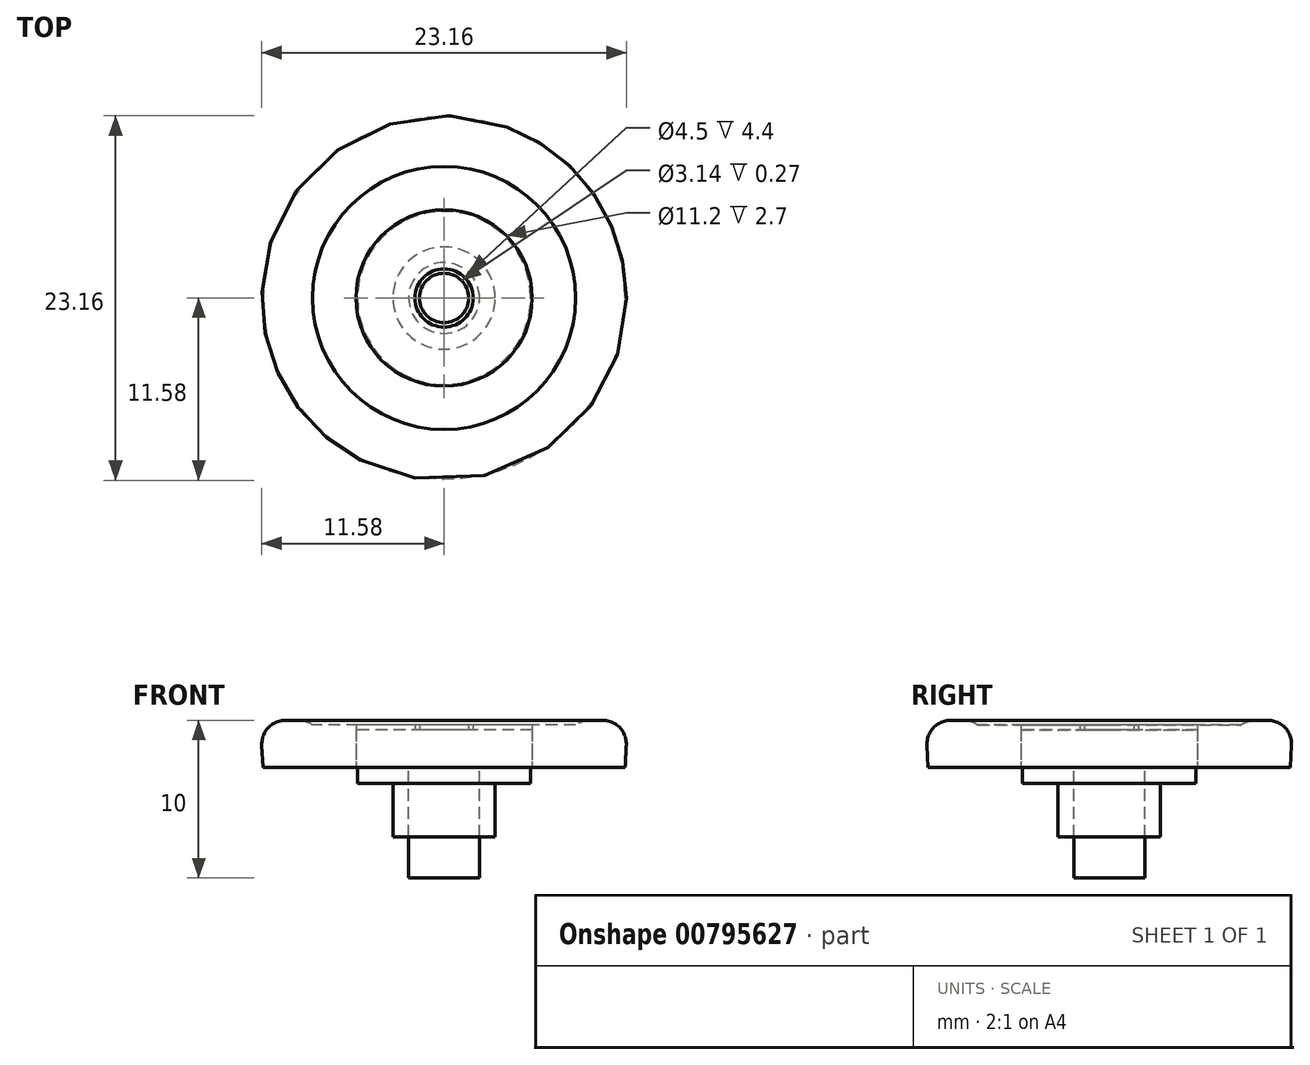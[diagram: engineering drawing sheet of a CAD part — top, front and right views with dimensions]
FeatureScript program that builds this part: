
annotation { "Feature Type Name" : "Feature", "Feature Type Description" : "" }
export const myFeature = defineFeature(function(context is Context, id is Id, definition is map)
    precondition{}
    {
        {
            var Q0;
            Q0=qCreatedBy(makeId("Top.planeOp"),FACE);
            var sketch = newSketch(context, id + "F0", { "sketchPlane" : qUnion([Q0])});
            skCircle(sketch, "E0", {"center": v(0, 0) * mm, "radius": 11.5 * mm});
            skCircle(sketch, "E1", {"center": v(0, 0) * mm, "radius": 8.5 * mm});
            skCircle(sketch, "E2", {"center": v(0, 0) * mm, "radius": 5.6 * mm});
            skSolve(sketch);
        }
        {
            var Q0;
            Q0=qSketchRegion(id+"F0",true);
            extrude(context, id + "F1", {"entities" : qUnion([Q0]), "depth" : 3 * mm, "offsetDistance" : 25 * mm, "hasDraft" : true, "draftAngle" : 3 * degree});
        }
        {
            var Q0;
            Q0=makeQuery(id+"F0.imprint","IMPRINT",FACE,{"disambiguationData":[TD([[makeQuery(id+"F0.imprint","IMPRINT",EDGE,{"derivedFrom":sQuery(id+"F0.wireOp",EDGE,"E1")}),1.0]])]});
            extrude(context, id + "F2", {"entities" : qUnion([Q0]), "operationType" : NewBodyOperationType.ADD, "depth" : 2.7 * mm, "offsetDistance" : 25 * mm});
        }
        {
            var Q0;
            Q0=makeQuery(id+"F0.imprint","IMPRINT",FACE,{"disambiguationData":[TD([[makeQuery(id+"F0.imprint","IMPRINT",EDGE,{"derivedFrom":sQuery(id+"F0.wireOp",EDGE,"sJWBEL4Q-zqKP-wKAH-Xvia-YZl9IQGTlxIB")}),1.0]])]});
            var Q1;
            Q1=makeQuery(id+"F0.imprint","IMPRINT",FACE,{"disambiguationData":[TD([[makeQuery(id+"F0.imprint","IMPRINT",EDGE,{"derivedFrom":sQuery(id+"F0.wireOp",EDGE,"W3Ua214L-QGfU-jLto-IY45-T6SqmYm5Pf0N")}),1.0]])]});
            var Q2;
            Q2=makeQuery(id+"F0.imprint","IMPRINT",FACE,{"disambiguationData":[TD([[makeQuery(id+"F0.imprint","IMPRINT",EDGE,{"derivedFrom":sQuery(id+"F0.wireOp",EDGE,"KE1PqsyT-DHGX-8diU-NURI-yFHnlOPL5x9j")}),1.0]])]});
            var Q3;
            Q3=makeQuery(id+"F0.imprint","IMPRINT",FACE,{"disambiguationData":[TD([[makeQuery(id+"F0.imprint","IMPRINT",EDGE,{"derivedFrom":sQuery(id+"F0.wireOp",EDGE,"93cc1e78-3582-4651-860f-33596dd8aeea")}),1.0]])]});
            var Q4;
            Q4=makeQuery(id+"F0.imprint","IMPRINT",FACE,{"disambiguationData":[TD([[makeQuery(id+"F0.imprint","IMPRINT",EDGE,{"derivedFrom":sQuery(id+"F0.wireOp",EDGE,"580936a7-a73b-495c-908d-01e9c6adc14b")}),1.0]])]});
            var Q5;
            Q5=makeQuery(id+"F0.imprint","IMPRINT",FACE,{"disambiguationData":[TD([[makeQuery(id+"F0.imprint","IMPRINT",EDGE,{"derivedFrom":sQuery(id+"F0.wireOp",EDGE,"914aee80-40cc-4c9e-a0ba-7517bd072fba")}),1.0]])]});
            var Q6;
            Q6=makeQuery(id+"F0.imprint","IMPRINT",FACE,{"disambiguationData":[TD([[makeQuery(id+"F0.imprint","IMPRINT",EDGE,{"derivedFrom":sQuery(id+"F0.wireOp",EDGE,"tJGHLqfq-XDhS-PHHt-wrfx-KiIFVS5NVcas")}),1.0]])]});
            var Q7;
            Q7=makeQuery(id+"F0.imprint","IMPRINT",FACE,{"disambiguationData":[TD([[makeQuery(id+"F0.imprint","IMPRINT",EDGE,{"derivedFrom":sQuery(id+"F0.wireOp",EDGE,"QfYnkFk0-Tl5y-BypX-IXop-PRvAgd9sKDpf")}),1.0]])]});
            var Q8;
            Q8=makeQuery(id+"F0.imprint","IMPRINT",FACE,{"disambiguationData":[TD([[makeQuery(id+"F0.imprint","IMPRINT",EDGE,{"derivedFrom":sQuery(id+"F0.wireOp",EDGE,"Y070iHcx-JKvN-373v-bcgJ-Ptq9Z7jqXRuu")}),1.0]])]});
            var Q9;
            {var subQ0=sQuery(id+"F0.wireOp",EDGE,"364aceb5-e4ae-42a2-838b-8d2f1a538a20");var subQ5=sQuery(id+"F0.wireOp",EDGE,"E2");var subQ8=makeQuery(id+"F0.imprint","INTERSECT",VERTEX,{"disambiguationData":[OD(0.0)],"derivedFrom":[subQ5,subQ0]});Q9=makeQuery(id+"F0.imprint","IMPRINT",FACE,{"disambiguationData":[TD([[makeQuery(id+"F0.imprint","IMPRINT",EDGE,{"disambiguationData":[TD([[subQ8,1.0]])],"derivedFrom":subQ5}),1.0]])]});}
            var Q10;
            {var subQ1=sQuery(id+"F0.wireOp",EDGE,"E2");var subQ3=sQuery(id+"F0.wireOp",EDGE,"240fa6d0-75f4-4649-a5dc-fb8ea6b493ce");var subQ4=makeQuery(id+"F0.imprint","INTERSECT",VERTEX,{"disambiguationData":[OD(0.0)],"derivedFrom":[subQ1,subQ3]});Q10=makeQuery(id+"F0.imprint","IMPRINT",FACE,{"disambiguationData":[TD([[makeQuery(id+"F0.imprint","IMPRINT",EDGE,{"disambiguationData":[TD([[subQ4,-1.0]])],"derivedFrom":subQ1}),1.0]])]});}
            var Q11;
            {var subQ0=sQuery(id+"F0.wireOp",EDGE,"a4363b79-0781-4621-b503-21fbbac03dd4");Q11=makeQuery(id+"F0.imprint","IMPRINT",FACE,{"disambiguationData":[TD([[makeQuery(id+"F0.imprint","IMPRINT",EDGE,{"derivedFrom":subQ0}),1.0]])]});}
            var Q12;
            Q12=makeQuery(id+"F0.imprint","IMPRINT",FACE,{"disambiguationData":[TD([[makeQuery(id+"F0.imprint","IMPRINT",EDGE,{"derivedFrom":sQuery(id+"F0.wireOp",EDGE,"dakPGjOR-qgw5-qXTv-UFbR-eR2Q9f3JjfMY")}),1.0]])]});
            var Q13;
            Q13=makeQuery(id+"F0.imprint","IMPRINT",FACE,{"disambiguationData":[TD([[makeQuery(id+"F0.imprint","IMPRINT",EDGE,{"derivedFrom":sQuery(id+"F0.wireOp",EDGE,"c86a8116-1d08-438b-9353-779b471d0a26")}),-1.0]])]});
            var Q14;
            {var subQ5=sQuery(id+"F0.wireOp",EDGE,"240fa6d0-75f4-4649-a5dc-fb8ea6b493ce");Q14=makeQuery(id+"F0.imprint","IMPRINT",FACE,{"disambiguationData":[TD([[makeQuery(id+"F0.imprint","IMPRINT",EDGE,{"derivedFrom":subQ5}),-1.0]])]});}
            var Q15;
            {var subQ0=sQuery(id+"F0.wireOp",EDGE,"cf34df1f-d6ec-4883-8101-f005d7a4a38d");Q15=makeQuery(id+"F0.imprint","IMPRINT",FACE,{"disambiguationData":[TD([[makeQuery(id+"F0.imprint","IMPRINT",EDGE,{"derivedFrom":subQ0}),-1.0]])]});}
            extrude(context, id + "F3", {"entities" : qUnion([Q0, Q1, Q2, Q3, Q4, Q5, Q6, Q7, Q8, Q9, Q10, Q11, Q12, Q13, Q14, Q15]), "depth" : 2.4 * mm, "offsetDistance" : 25 * mm});
        }
        {
            var Q0;
            Q0=makeQuery(id+"F1.opExtrude","CAP_EDGE",EDGE,{"disambiguationData":[OSD([sQuery(id+"F0.wireOp",EDGE,"E1")])],"isStart":false});
            var Q1;
            Q1=makeQuery(id+"F1.opExtrude","CAP_EDGE",EDGE,{"disambiguationData":[OSD([sQuery(id+"F0.wireOp",EDGE,"E0")])],"isStart":false});
            fillet(context, id + "F4", {"entities" : qUnion([Q0, Q1]), "radius" : 1.5 * mm, "tangentPropagation" : true, "allowEdgeOverflow" : false});
        }
        {
            var Q0;
            Q0=qCreatedBy(makeId("Top.planeOp"),FACE);
            var sketch = newSketch(context, id + "F5", { "sketchPlane" : qUnion([Q0])});
            skCircle(sketch, "E3", {"center": v(0, 0) * mm, "radius": 5.5 * mm});
            skCircle(sketch, "E4", {"center": v(0, 0) * mm, "radius": 3.25 * mm});
            skCircle(sketch, "E5", {"center": v(0, 0) * mm, "radius": 2.25 * mm});
            skSolve(sketch);
        }
        {
            var Q0;
            Q0=qSketchRegion(id+"F5",true);
            extrude(context, id + "F6", {"entities" : qUnion([Q0]), "operationType" : NewBodyOperationType.ADD, "oppositeDirection" : true, "depth" : 1 * mm, "offsetDistance" : 25 * mm});
        }
        {
            var Q0;
            Q0=makeQuery(id+"F5.imprint","IMPRINT",FACE,{"disambiguationData":[TD([[makeQuery(id+"F5.imprint","IMPRINT",EDGE,{"derivedFrom":sQuery(id+"F5.wireOp",EDGE,"E4")}),1.0]])]});
            extrude(context, id + "F7", {"entities" : qUnion([Q0]), "operationType" : NewBodyOperationType.ADD, "oppositeDirection" : true, "depth" : 4.4 * mm, "offsetDistance" : 25 * mm});
        }
        {
            var Q0;
            Q0=makeQuery(id+"F5.imprint","IMPRINT",FACE,{"disambiguationData":[TD([[makeQuery(id+"F5.imprint","IMPRINT",EDGE,{"derivedFrom":sQuery(id+"F5.wireOp",EDGE,"E5")}),1.0]])]});
            extrude(context, id + "F8", {"entities" : qUnion([Q0]), "oppositeDirection" : true, "depth" : 7 * mm, "offsetDistance" : 25 * mm});
        }
        {
            var Q0;
            Q0=qCreatedBy(makeId("Top.planeOp"),FACE);
            cPlane(context, id + "F9", {"entities" : qUnion([Q0]), "cplaneType" : CPlaneType.OFFSET, "offset" : 2.4 * mm, "width" : 150 * mm, "height" : 150 * mm});
        }
        {
            var Q0;
            Q0=qCreatedBy(id+"F9.planeOp",FACE);
            var sketch = newSketch(context, id + "F10", { "sketchPlane" : qUnion([Q0])});
            skCircle(sketch, "E6", {"center": v(0, 0) * mm, "radius": 1.85 * mm});
            skCircle(sketch, "E7", {"center": v(0, 0) * mm, "radius": 1.57 * mm});
            skCircle(sketch, "E8", {"center": v(0, 0) * mm, "radius": 5.6 * mm});
            skFitSpline(sketch, "E9", {"points": [v(1.78, -0.5) * mm, v(1.79, -0.56) * mm, v(1.81, -0.61) * mm, v(1.9, -0.7) * mm, v(2.12, -0.88) * mm, v(2.47, -1.1) * mm, v(2.86, -1.37) * mm, v(3.48, -1.75) * mm, v(4.06, -2.14) * mm, v(4.51, -2.4) * mm, v(4.63, -2.44) * mm, v(4.76, -2.46) * mm, v(4.87, -2.44) * mm, v(4.98, -2.4) * mm, v(5.1, -2.3) * mm], "startDerivative": vector(-0.8, -2.81) * mm, "endDerivative": vector(1.02, 2.24) * mm});
            skFitSpline(sketch, "E10", {"points": [v(-1.07, -1.51) * mm, v(-1.2, -1.46) * mm, v(-1.28, -1.46) * mm, v(-1.4, -1.48) * mm, v(-1.66, -1.6) * mm, v(-2.02, -1.8) * mm, v(-2.43, -2.03) * mm, v(-3.06, -2.4) * mm, v(-3.68, -2.73) * mm, v(-4.11, -3) * mm, v(-4.22, -3.08) * mm, v(-4.3, -3.18) * mm, v(-4.36, -3.3) * mm, v(-4.37, -3.42) * mm, v(-4.3, -3.58) * mm], "startDerivative": vector(-2.5, 1.82) * mm, "endDerivative": vector(2.87, -3.5) * mm});
            skFitSpline(sketch, "E11", {"points": [v(0.97, -1.57) * mm, v(1.06, -1.54) * mm, v(1.16, -1.52) * mm, v(1.3, -1.5) * mm, v(1.46, -1.55) * mm, v(1.84, -1.76) * mm, v(2.37, -2.05) * mm, v(2.81, -2.3) * mm, v(3.45, -2.66) * mm, v(4, -2.98) * mm, v(4.14, -3.06) * mm, v(4.24, -3.15) * mm, v(4.3, -3.27) * mm, v(4.33, -3.38) * mm, v(4.31, -3.53) * mm, v(4.25, -3.64) * mm, v(4.25, -3.64) * mm], "startDerivative": vector(2.43, 1.54) * mm, "endDerivative": vector(0.65, 0.76) * mm});
            skCircle(sketch, "E12", {"center": v(2.1, -1.4) * mm, "radius": 0.22 * mm});
            skCircle(sketch, "E13", {"center": v(3.06, -1.98) * mm, "radius": 0.18 * mm});
            skCircle(sketch, "E14", {"center": v(3.83, -2.46) * mm, "radius": 0.14 * mm});
            skLineSegment(sketch, "E15", {"start": v(1.53, -1.04) * mm, "end": v(4.73, -3) * mm, "construction": true});
            skFitSpline(sketch, "E16", {"points": [v(-1.83, -0.27) * mm, v(-1.83, -0.48) * mm, v(-1.86, -0.55) * mm, v(-1.93, -0.65) * mm, v(-2.05, -0.77) * mm, v(-2.4, -1.03) * mm, v(-2.9, -1.37) * mm, v(-3.39, -1.67) * mm, v(-3.91, -2) * mm, v(-4.36, -2.26) * mm, v(-4.67, -2.42) * mm, v(-4.86, -2.46) * mm, v(-5, -2.43) * mm, v(-5.25, -1.96) * mm], "startDerivative": vector(1.36, -7.17) * mm, "endDerivative": vector(-3.92, 9.14) * mm});
            skCircle(sketch, "E17", {"center": v(-2.18, -1.4) * mm, "radius": 0.22 * mm});
            skCircle(sketch, "E18", {"center": v(-3.14, -1.99) * mm, "radius": 0.18 * mm});
            skCircle(sketch, "E19", {"center": v(-3.91, -2.46) * mm, "radius": 0.14 * mm});
            skLineSegment(sketch, "E20", {"start": v(-1.54, -1.02) * mm, "end": v(-4.76, -2.95) * mm, "construction": true});
            skFitSpline(sketch, "E21", {"points": [v(-0.72, 1.7) * mm, v(-0.59, 1.81) * mm, v(-0.52, 1.91) * mm, v(-0.47, 2.08) * mm, v(-0.46, 2.3) * mm, v(-0.45, 2.72) * mm, v(-0.44, 3.2) * mm, v(-0.44, 3.91) * mm, v(-0.42, 4.62) * mm, v(-0.44, 5.13) * mm, v(-0.47, 5.26) * mm, v(-0.51, 5.38) * mm, v(-0.59, 5.46) * mm, v(-0.7, 5.53) * mm, v(-0.82, 5.54) * mm], "startDerivative": vector(2.8, 0.8) * mm, "endDerivative": vector(-2.44, -0.32) * mm});
            skFitSpline(sketch, "E22", {"points": [v(0.74, 1.7) * mm, v(0.67, 1.75) * mm, v(0.6, 1.83) * mm, v(0.51, 1.94) * mm, v(0.47, 2.1) * mm, v(0.44, 2.53) * mm, v(0.43, 3.14) * mm, v(0.42, 3.65) * mm, v(0.4, 4.38) * mm, v(0.39, 5.1) * mm, v(0.4, 5.24) * mm, v(0.44, 5.37) * mm, v(0.5, 5.45) * mm, v(0.58, 5.5) * mm, v(0.67, 5.53) * mm, v(0.84, 5.54) * mm], "startDerivative": vector(-1.87, 1.36) * mm, "endDerivative": vector(4.35, -0.63) * mm});
            skCircle(sketch, "E23", {"center": v(0, 2.56) * mm, "radius": 0.22 * mm});
            skCircle(sketch, "E24", {"center": v(0, 3.73) * mm, "radius": 0.18 * mm});
            skCircle(sketch, "E25", {"center": v(0, 4.59) * mm, "radius": 0.14 * mm});
            skLineSegment(sketch, "E26", {"start": v(0, 1.85) * mm, "end": v(0, 5.6) * mm, "construction": true});
            skCircle(sketch, "E27", {"center": v(0, 0) * mm, "radius": 5.95 * mm});
            skFitSpline(sketch, "E28", {"points": [v(-1.05, -0.83) * mm, v(-1.13, -0.72) * mm, v(-1.22, -0.56) * mm, v(-1.28, -0.37) * mm, v(-1.3, -0.17) * mm, v(-1.32, 0.02) * mm, v(-1.3, 0.2) * mm, v(-1.22, 0.43) * mm, v(-1.13, 0.6) * mm, v(-1, 0.78) * mm, v(-0.85, 0.93) * mm, v(-0.72, 1.04) * mm, v(-0.56, 1.13) * mm, v(-0.45, 1.18) * mm, v(-0.45, 1.18) * mm], "startDerivative": vector(-1.28, 1.58) * mm, "endDerivative": vector(-0.6, -0.06) * mm});
            skFitSpline(sketch, "E29", {"points": [v(-0.64, 0.92) * mm, v(-0.75, 0.85) * mm, v(-0.84, 0.76) * mm, v(-0.93, 0.66) * mm, v(-1.01, 0.53) * mm, v(-1.08, 0.36) * mm, v(-1.1, 0.21) * mm, v(-1.12, 0.05) * mm, v(-1.12, -0.13) * mm], "startDerivative": vector(-1.01, -0.52) * mm, "endDerivative": vector(0, -1.33) * mm});
            skFitSpline(sketch, "E30", {"points": [v(-1.12, -0.13) * mm, v(-0.9, -0.13) * mm, v(-0.65, -0.13) * mm], "startDerivative": vector(0.46, 0) * mm, "endDerivative": vector(0.47, 0) * mm});
            skFitSpline(sketch, "E31", {"points": [v(-0.65, -0.13) * mm, v(-0.65, 0.18) * mm, v(-0.65, 0.52) * mm, v(-0.64, 0.92) * mm], "startDerivative": vector(0, 0.98) * mm, "endDerivative": vector(0.04, 1.13) * mm});
            skFitSpline(sketch, "E32", {"points": [v(-0.45, 1.18) * mm, v(-0.45, 0.64) * mm, v(-0.45, -0.19) * mm, v(-0.45, -0.76) * mm, v(-0.45, -1.2) * mm], "startDerivative": vector(0, -2.1) * mm, "endDerivative": vector(0, -2.03) * mm});
            skFitSpline(sketch, "E33", {"points": [v(-0.45, -1.2) * mm, v(-0.53, -1.16) * mm, v(-0.64, -1.11) * mm], "startDerivative": vector(-0.17, 0.1) * mm, "endDerivative": vector(-0.22, 0.1) * mm});
            skFitSpline(sketch, "E34", {"points": [v(-0.64, -1.11) * mm, v(-0.64, -0.76) * mm, v(-0.64, -0.5) * mm, v(-0.64, -0.29) * mm], "startDerivative": vector(0, 0.95) * mm, "endDerivative": vector(0, 0.7) * mm});
            skFitSpline(sketch, "E35", {"points": [v(-0.64, -0.29) * mm, v(-0.85, -0.29) * mm, v(-1.05, -0.29) * mm], "startDerivative": vector(-0.4, 0) * mm, "endDerivative": vector(-0.41, 0) * mm});
            skFitSpline(sketch, "E36", {"points": [v(-1.05, -0.29) * mm, v(-1.04, -0.4) * mm, v(-1.01, -0.5) * mm, v(-0.95, -0.6) * mm, v(-0.9, -0.68) * mm], "startDerivative": vector(0.02, -0.66) * mm, "endDerivative": vector(0.26, -0.3) * mm});
            skFitSpline(sketch, "E37", {"points": [v(-0.9, -0.68) * mm, v(-0.97, -0.75) * mm, v(-1.05, -0.83) * mm], "startDerivative": vector(-0.17, -0.14) * mm, "endDerivative": vector(-0.15, -0.16) * mm});
            skSolve(sketch);
        }
        {
            var Q0;
            Q0=makeQuery(id+"F10.imprint","IMPRINT",FACE,{"disambiguationData":[TD([[makeQuery(id+"F10.imprint","IMPRINT",EDGE,{"derivedFrom":sQuery(id+"F10.wireOp",EDGE,"E7")}),-1.0]])]});
            var Q1;
            {var subQ0=sQuery(id+"F10.wireOp",EDGE,"E9");Q1=makeQuery(id+"F10.imprint","IMPRINT",FACE,{"disambiguationData":[TD([[makeQuery(id+"F10.imprint","IMPRINT",EDGE,{"derivedFrom":subQ0}),-1.0]])]});}
            var Q2;
            {var subQ0=sQuery(id+"F10.wireOp",EDGE,"E22");Q2=makeQuery(id+"F10.imprint","IMPRINT",FACE,{"disambiguationData":[TD([[makeQuery(id+"F10.imprint","IMPRINT",EDGE,{"derivedFrom":subQ0}),1.0]])]});}
            var Q3;
            {var subQ5=sQuery(id+"F10.wireOp",EDGE,"E10");Q3=makeQuery(id+"F10.imprint","IMPRINT",FACE,{"disambiguationData":[TD([[makeQuery(id+"F10.imprint","IMPRINT",EDGE,{"derivedFrom":subQ5}),-1.0]])]});}
            extrude(context, id + "F11", {"entities" : qUnion([Q0, Q1, Q2, Q3]), "depth" : 0.3 * mm, "offsetDistance" : 25 * mm});
        }
        {
            var Q0;
            Q0=makeQuery(id+"F11.opExtrude","CAP_EDGE",EDGE,{"disambiguationData":[OSD([sQuery(id+"F10.wireOp",EDGE,"E10")])],"isStart":false});
            var Q1;
            Q1=makeQuery(id+"F11.opExtrude","CAP_EDGE",EDGE,{"disambiguationData":[OSD([sQuery(id+"F10.wireOp",EDGE,"E9")])],"isStart":false});
            var Q2;
            {var subQ0=sQuery(id+"F10.wireOp",EDGE,"E6");Q2=makeQuery(id+"F11.opExtrude","CAP_EDGE",EDGE,{"disambiguationData":[OSD([subQ0]),TDD([makeQuery(id+"F10.imprint","IMPRINT",EDGE,{"disambiguationData":[TD([[makeQuery(id+"F10.imprint","INTERSECT",VERTEX,{"derivedFrom":[subQ0,sQuery(id+"F10.wireOp",EDGE,"E9")]}),-1.0]])],"derivedFrom":subQ0})])],"isStart":false});}
            var Q3;
            Q3=makeQuery(id+"F11.opExtrude","CAP_EDGE",EDGE,{"disambiguationData":[OSD([sQuery(id+"F10.wireOp",EDGE,"E22")])],"isStart":false});
            var Q4;
            Q4=makeQuery(id+"F11.opExtrude","CAP_EDGE",EDGE,{"disambiguationData":[OSD([sQuery(id+"F10.wireOp",EDGE,"E21")])],"isStart":false});
            var Q5;
            {var subQ0=sQuery(id+"F10.wireOp",EDGE,"E6");Q5=makeQuery(id+"F11.opExtrude","CAP_EDGE",EDGE,{"disambiguationData":[OSD([subQ0]),TDD([makeQuery(id+"F10.imprint","IMPRINT",EDGE,{"disambiguationData":[TD([[makeQuery(id+"F10.imprint","INTERSECT",VERTEX,{"disambiguationData":[OD(0.0)],"derivedFrom":[subQ0,sQuery(id+"F10.wireOp",EDGE,"E16")]}),1.0]])],"derivedFrom":subQ0})])],"isStart":false});}
            var Q6;
            Q6=makeQuery(id+"F11.opExtrude","CAP_EDGE",EDGE,{"disambiguationData":[OSD([sQuery(id+"F10.wireOp",EDGE,"E16")])],"isStart":false});
            var Q7;
            Q7=makeQuery(id+"F11.opExtrude","CAP_EDGE",EDGE,{"disambiguationData":[OSD([sQuery(id+"F10.wireOp",EDGE,"E11")])],"isStart":false});
            var Q8;
            {var subQ0=sQuery(id+"F10.wireOp",EDGE,"E6");var subQ1=makeQuery(id+"F10.imprint","IMPRINT",VERTEX,{"disambiguationData":[OD(1.0)],"derivedFrom":subQ0});var subQ2=makeQuery(id+"F10.imprint","IMPRINT",VERTEX,{"disambiguationData":[OD(0.0)],"derivedFrom":subQ0});Q8=makeQuery(id+"F11.opExtrude","CAP_EDGE",EDGE,{"disambiguationData":[OSD([subQ0]),TDD([makeQuery(id+"F10.imprint","IMPRINT",EDGE,{"disambiguationData":[TD([[subQ2,1.0]])],"derivedFrom":subQ0}),makeQuery(id+"F10.imprint","IMPRINT",EDGE,{"disambiguationData":[TD([[subQ2,-1.0]])],"derivedFrom":subQ0}),makeQuery(id+"F10.imprint","IMPRINT",EDGE,{"disambiguationData":[TD([[subQ1,-1.0]])],"derivedFrom":subQ0})])],"isStart":false});}
            var Q9;
            Q9=makeQuery(id+"F11.opExtrude","CAP_EDGE",EDGE,{"disambiguationData":[OSD([sQuery(id+"F10.wireOp",EDGE,"E7")])],"isStart":false});
            fillet(context, id + "F12", {"entities" : qUnion([Q0, Q1, Q2, Q3, Q4, Q5, Q6, Q7, Q8, Q9]), "radius" : 0.03 * mm, "tangentPropagation" : true, "allowEdgeOverflow" : false});
        }
    });
